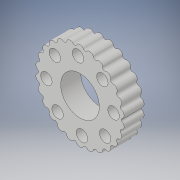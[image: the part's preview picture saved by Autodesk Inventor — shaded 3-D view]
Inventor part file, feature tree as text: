
AUTODESK INVENTOR PART (.ipt)
format: ipt  version: 2019.4 (Build 234330000, 330)  size: 320,000 bytes
history: native  units: mm
features: extrude x2, sketch x2, pattern_circular x1, other x1, projected_geometry x1
ambient origin geometry x8: Origin, YZ Plane, XZ Plane, XY Plane, X Axis, Y Axis, Z Axis, Center Point
bodies: Solid1 (feature_tree)
feature tree (7):
  extrude  "Extrusion1"  Depth=8.0mm
  extrude  "Extrusion2"  Depth=5.0mm
  pattern_circular  "Circular Pattern1"  Count=8 Angle=360.0deg
  sketch  "Sketch1"  dims[d0=0.0mm d1=3600.0mm d2=8.0mm]
  other  "2D Equation Curve1"
  sketch  "Sketch2"  dims[d3=23.5mm d4=0.581776mm d5=80.0mm d7=360.0deg d9=27.0mm d10=14.0mm d11=0.0mm d12=7.0mm d13=5.0mm d14=0.0mm d15=80.0mm d16=360.0deg]
  projected_geometry  "Projected Loop1"
